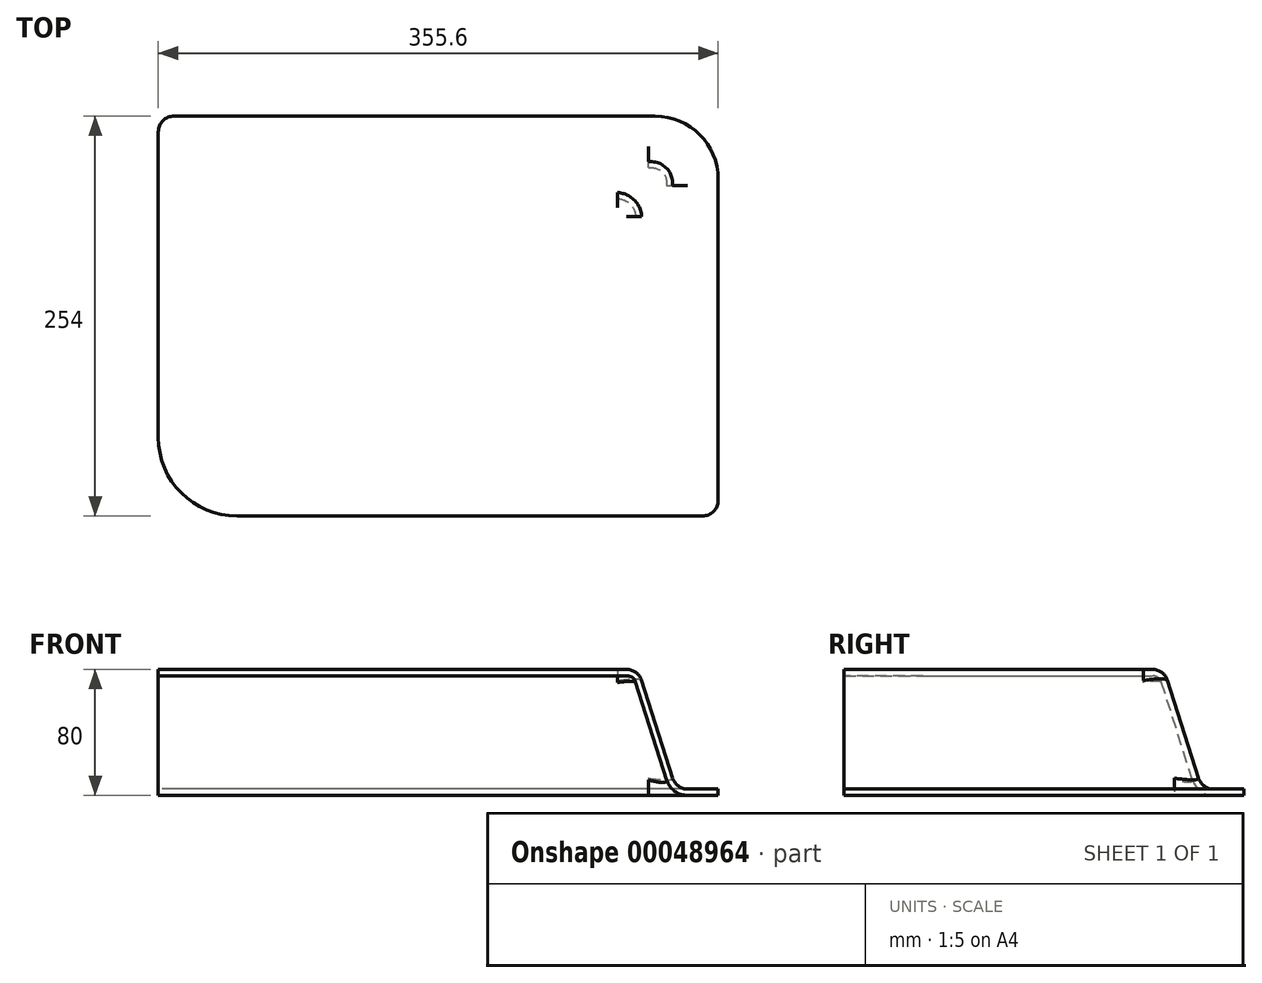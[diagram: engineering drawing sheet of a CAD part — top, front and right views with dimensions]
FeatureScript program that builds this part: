
annotation { "Feature Type Name" : "Feature", "Feature Type Description" : "" }
export const myFeature = defineFeature(function(context is Context, id is Id, definition is map)
    precondition{}
    {
        {
            var Q0;
            Q0=qCreatedBy(makeId("Top.planeOp"),FACE);
            var sketch = newSketch(context, id + "F0", { "sketchPlane" : qUnion([Q0])});
            skLineSegment(sketch, "E0.rect.bottom", {"start": v(177.8, -127) * mm, "end": v(-177.8, -127) * mm});
            skLineSegment(sketch, "E0.rect.top", {"start": v(177.8, 127) * mm, "end": v(-177.8, 127) * mm});
            skLineSegment(sketch, "E0.rect.left", {"start": v(177.8, -127) * mm, "end": v(177.8, 127) * mm});
            skLineSegment(sketch, "E0.rect.right", {"start": v(-177.8, -127) * mm, "end": v(-177.8, 127) * mm});
            skPoint(sketch, "E0.rect.middle", {"position": v(0, 0) * mm});
            skSolve(sketch);
        }
        {
            var Q0;
            Q0=qCreatedBy(makeId("Top.planeOp"),FACE);
            cPlane(context, id + "F1", {"entities" : qUnion([Q0]), "cplaneType" : CPlaneType.OFFSET, "offset" : 80 * mm, "width" : 150 * mm, "height" : 150 * mm});
        }
        {
            var Q0;
            Q0=qCreatedBy(id+"F1.planeOp",FACE);
            var sketch = newSketch(context, id + "F2", { "sketchPlane" : qUnion([Q0])});
            skLineSegment(sketch, "E1.bottom", {"start": v(-177.8, -127) * mm, "end": v(127, -127) * mm});
            skLineSegment(sketch, "E1.top", {"start": v(-177.8, 76.2) * mm, "end": v(127, 76.2) * mm});
            skLineSegment(sketch, "E1.left", {"start": v(-177.8, -127) * mm, "end": v(-177.8, 76.2) * mm});
            skLineSegment(sketch, "E1.right", {"start": v(127, -127) * mm, "end": v(127, 76.2) * mm});
            skSolve(sketch);
        }
        {
            var Q0;
            Q0=qCreatedBy(makeId("Top.planeOp"),FACE);
            var sketch = newSketch(context, id + "F3", { "sketchPlane" : qUnion([Q0])});
            skLineSegment(sketch, "E2.bottom", {"start": v(-177.8, -127) * mm, "end": v(152.4, -127) * mm});
            skLineSegment(sketch, "E2.top", {"start": v(-177.8, 101.6) * mm, "end": v(152.4, 101.6) * mm});
            skLineSegment(sketch, "E2.left", {"start": v(-177.8, -127) * mm, "end": v(-177.8, 101.6) * mm});
            skLineSegment(sketch, "E2.right", {"start": v(152.4, -127) * mm, "end": v(152.4, 101.6) * mm});
            skSolve(sketch);
        }
        {
            var Q0;
            Q0=makeQuery(id+"F3.imprint","IMPRINT",FACE,{"disambiguationData":[TD([[makeQuery(id+"F3.imprint","IMPRINT",EDGE,{"derivedFrom":sQuery(id+"F3.wireOp",EDGE,"E2.bottom")}),1.0]])]});
            var Q1;
            Q1=makeQuery(id+"F2.imprint","IMPRINT",FACE,{"disambiguationData":[TD([[makeQuery(id+"F2.imprint","IMPRINT",EDGE,{"derivedFrom":sQuery(id+"F2.wireOp",EDGE,"E1.bottom")}),1.0]])]});
            loft(context, id + "F4", {"sheetProfilesArray" : [{ "sheetProfileEntities" : qUnion([Q0]) }, { "sheetProfileEntities" : qUnion([Q1]) }]});
        }
        {
            var Q0;
            Q0 = qSketchRegion(id + "F0", true);
            extrude(context, id + "F5", {"entities" : qUnion([Q0]), "operationType" : NewBodyOperationType.ADD, "depth" : 4 * mm});
        }
        {
            var Q0;
            Q0=makeQuery(id+"F4.opLoft","SWEPT_EDGE",EDGE,{"disambiguationData":[OSD([sQuery(id+"F2.wireOp",EDGE,"E1.top"),sQuery(id+"F2.wireOp",EDGE,"E1.right"),sQuery(id+"F3.wireOp",EDGE,"E2.top"),sQuery(id+"F3.wireOp",EDGE,"E2.right")])]});
            fillet(context, id + "F6", {"entities" : qUnion([Q0]), "radius" : 16 * mm, "tangentPropagation" : true, "allowEdgeOverflow" : false});
        }
        {
            var Q0;
            Q0=makeQuery(id+"F5.boolean.opBoolean","INTERSECT",EDGE,{"derivedFrom":[makeQuery(id+"F4.opLoft","SWEPT_FACE",FACE,{"disambiguationData":[OSD([sQuery(id+"F2.wireOp",EDGE,"E1.bottom"),sQuery(id+"F2.wireOp",EDGE,"E1.top"),sQuery(id+"F2.wireOp",EDGE,"E1.right"),sQuery(id+"F3.wireOp",EDGE,"E2.bottom"),sQuery(id+"F3.wireOp",EDGE,"E2.top"),sQuery(id+"F3.wireOp",EDGE,"E2.right")])]}),makeQuery(id+"F5.opExtrude","CAP_FACE",FACE,{"disambiguationData":[OSD([sQuery(id+"F0.wireOp",EDGE,"E0.rect.bottom"),sQuery(id+"F0.wireOp",EDGE,"E0.rect.top"),sQuery(id+"F0.wireOp",EDGE,"E0.rect.left"),sQuery(id+"F0.wireOp",EDGE,"E0.rect.right")])],"isStart":false})]});
            var Q1;
            Q1=makeQuery(id+"F4.opLoft","MID_CAP_EDGE",EDGE,{"disambiguationData":[OSD([sQuery(id+"F2.wireOp",EDGE,"E1.bottom"),sQuery(id+"F2.wireOp",EDGE,"E1.top"),sQuery(id+"F2.wireOp",EDGE,"E1.right")])],"capPos":1.0});
            fillet(context, id + "F7", {"entities" : qUnion([Q0, Q1]), "radius" : 10 * mm, "tangentPropagation" : true, "allowEdgeOverflow" : false});
        }
        {
            var Q0;
            Q0=makeQuery(id+"F4.opLoft","SWEPT_EDGE",EDGE,{"disambiguationData":[OSD([sQuery(id+"F2.wireOp",EDGE,"E1.bottom"),sQuery(id+"F2.wireOp",EDGE,"E1.left"),sQuery(id+"F3.wireOp",EDGE,"E2.bottom"),sQuery(id+"F3.wireOp",EDGE,"E2.left")])]});
            fillet(context, id + "F8", {"entities" : qUnion([Q0]), "radius" : 50 * mm, "tangentPropagation" : true, "allowEdgeOverflow" : false});
        }
        {
            var Q0;
            Q0=makeQuery(id+"F5.opExtrude","SWEPT_EDGE",EDGE,{"disambiguationData":[OSD([sQuery(id+"F0.wireOp",EDGE,"E0.rect.top"),sQuery(id+"F0.wireOp",EDGE,"E0.rect.right")])]});
            var Q1;
            Q1=makeQuery(id+"F5.opExtrude","SWEPT_EDGE",EDGE,{"disambiguationData":[OSD([sQuery(id+"F0.wireOp",EDGE,"E0.rect.bottom"),sQuery(id+"F0.wireOp",EDGE,"E0.rect.left")])]});
            fillet(context, id + "F9", {"entities" : qUnion([Q0, Q1]), "radius" : 10 * mm, "tangentPropagation" : true, "allowEdgeOverflow" : false});
        }
        {
            var Q0;
            Q0=makeQuery(id+"F5.boolean.opBoolean","MERGE",FACE,{"derivedFrom":[makeQuery(id+"F4.opLoft","CAP_FACE",FACE,{"disambiguationData":[OSD([makeQuery(id+"F3.imprint","IMPRINT",FACE,{"disambiguationData":[TD([[makeQuery(id+"F3.imprint","IMPRINT",EDGE,{"derivedFrom":sQuery(id+"F3.wireOp",EDGE,"E2.bottom")}),1.0]])]})])],"isStart":true}),makeQuery(id+"F5.opExtrude","CAP_FACE",FACE,{"disambiguationData":[OSD([sQuery(id+"F0.wireOp",EDGE,"E0.rect.bottom"),sQuery(id+"F0.wireOp",EDGE,"E0.rect.top"),sQuery(id+"F0.wireOp",EDGE,"E0.rect.left"),sQuery(id+"F0.wireOp",EDGE,"E0.rect.right")])],"isStart":true})]});
            var Q1;
            Q1=makeQuery(id+"F5.boolean.opBoolean","MERGE",FACE,{"derivedFrom":[makeQuery(id+"F4.opLoft","SWEPT_FACE",FACE,{"disambiguationData":[OSD([sQuery(id+"F2.wireOp",EDGE,"E1.bottom"),sQuery(id+"F2.wireOp",EDGE,"E1.left"),sQuery(id+"F2.wireOp",EDGE,"E1.right"),sQuery(id+"F3.wireOp",EDGE,"E2.bottom"),sQuery(id+"F3.wireOp",EDGE,"E2.left"),sQuery(id+"F3.wireOp",EDGE,"E2.right")])]}),makeQuery(id+"F5.opExtrude","SWEPT_FACE",FACE,{"disambiguationData":[OSD([sQuery(id+"F0.wireOp",EDGE,"E0.rect.bottom")])]})]});
            var Q2;
            Q2=makeQuery(id+"F5.boolean.opBoolean","MERGE",FACE,{"derivedFrom":[makeQuery(id+"F4.opLoft","SWEPT_FACE",FACE,{"disambiguationData":[OSD([sQuery(id+"F2.wireOp",EDGE,"E1.bottom"),sQuery(id+"F2.wireOp",EDGE,"E1.top"),sQuery(id+"F2.wireOp",EDGE,"E1.left"),sQuery(id+"F3.wireOp",EDGE,"E2.bottom"),sQuery(id+"F3.wireOp",EDGE,"E2.top"),sQuery(id+"F3.wireOp",EDGE,"E2.left")])]}),makeQuery(id+"F5.opExtrude","SWEPT_FACE",FACE,{"disambiguationData":[OSD([sQuery(id+"F0.wireOp",EDGE,"E0.rect.right")])]})]});
            var Q3;
            Q3=makeQuery(id+"F8.opFillet","BLEND_FACE",FACE,{"disambiguationData":[OSD([sQuery(id+"F2.wireOp",EDGE,"E1.bottom"),sQuery(id+"F2.wireOp",EDGE,"E1.left"),sQuery(id+"F3.wireOp",EDGE,"E2.bottom"),sQuery(id+"F3.wireOp",EDGE,"E2.left")])]});
            shell(context, id + "F10", {"entities" : qUnion([Q0, Q1, Q2, Q3]), "thickness" : 4 * mm});
        }
        {
            var Q0;
            Q0=makeQuery(id+"F5.opExtrude","SWEPT_EDGE",EDGE,{"disambiguationData":[OSD([sQuery(id+"F0.wireOp",EDGE,"E0.rect.top"),sQuery(id+"F0.wireOp",EDGE,"E0.rect.left")])]});
            fillet(context, id + "F11", {"entities" : qUnion([Q0]), "radius" : 40 * mm, "tangentPropagation" : true, "allowEdgeOverflow" : false});
        }
    });
